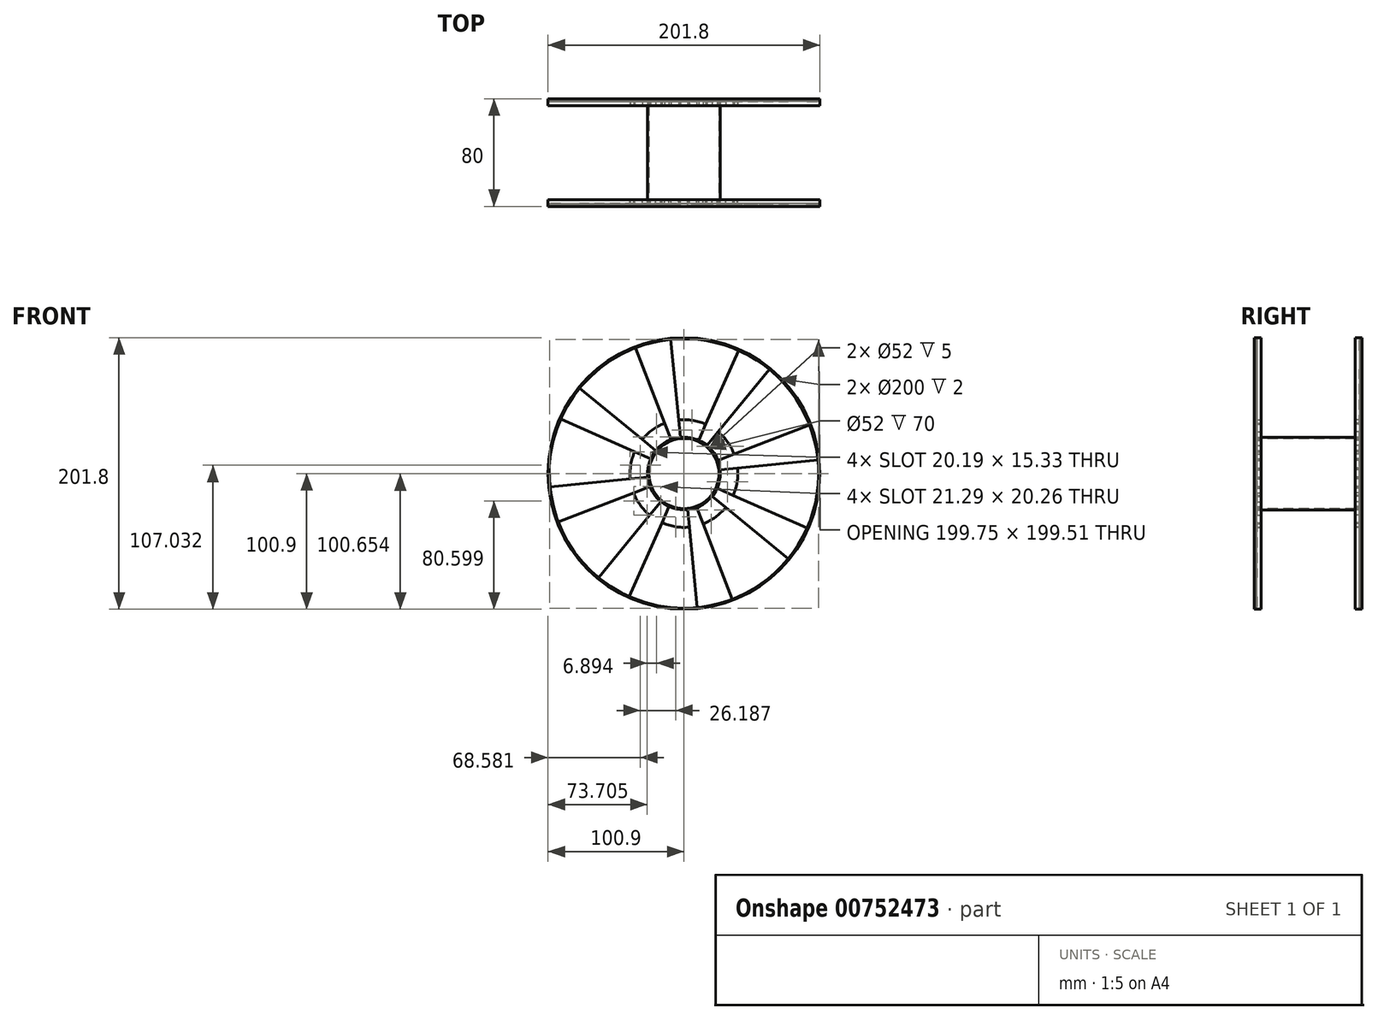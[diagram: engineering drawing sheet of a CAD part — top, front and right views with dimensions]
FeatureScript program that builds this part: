
annotation { "Feature Type Name" : "Feature", "Feature Type Description" : "" }
export const myFeature = defineFeature(function(context is Context, id is Id, definition is map)
    precondition{}
    {
        {
            var Q0;
            Q0=qCreatedBy(makeId("Front.planeOp"),FACE);
            var sketch = newSketch(context, id + "F0", { "sketchPlane" : qUnion([Q0])});
            skCircle(sketch, "E0", {"center": v(0, 0) * mm, "radius": 27 * mm});
            skCircle(sketch, "E1", {"center": v(0, 0) * mm, "radius": 100 * mm});
            skCircle(sketch, "E2", {"center": v(0, 0) * mm, "radius": 40 * mm});
            skLineSegment(sketch, "E3", {"start": v(-20.92, 17.06) * mm, "end": v(-30.95, 25.34) * mm});
            skLineSegment(sketch, "E4", {"start": v(-14.38, 37.33) * mm, "end": v(-9.65, 25.22) * mm});
            skCircle(sketch, "E5", {"center": v(0, 0) * mm, "radius": 100.9 * mm});
            skPoint(sketch, "E6.center", {"position": v(0, -0.02) * mm});
            skLineSegment(sketch, "E7", {"start": v(-14.38, 37.33) * mm, "end": v(-35.95, 93.32) * mm});
            skLineSegment(sketch, "E8", {"start": v(-30.95, 25.34) * mm, "end": v(-77.37, 63.36) * mm});
            skLineSegment(sketch, "E9.1.0", {"start": v(-36.56, 16.23) * mm, "end": v(-91.4, 40.57) * mm});
            skLineSegment(sketch, "E9.1.1", {"start": v(-39.8, -3.96) * mm, "end": v(-99.5, -9.9) * mm});
            skLineSegment(sketch, "E9.1.2", {"start": v(-26.86, -2.73) * mm, "end": v(-39.8, -3.96) * mm});
            skLineSegment(sketch, "E9.1.3", {"start": v(-36.56, 16.23) * mm, "end": v(-24.66, 11) * mm});
            skLineSegment(sketch, "E9.2.0", {"start": v(-37.33, -14.38) * mm, "end": v(-93.32, -35.95) * mm});
            skLineSegment(sketch, "E9.2.1", {"start": v(-25.34, -30.95) * mm, "end": v(-63.36, -77.37) * mm});
            skLineSegment(sketch, "E9.2.2", {"start": v(-17.06, -20.92) * mm, "end": v(-25.34, -30.95) * mm});
            skLineSegment(sketch, "E9.2.3", {"start": v(-37.33, -14.38) * mm, "end": v(-25.22, -9.65) * mm});
            skLineSegment(sketch, "E9.3.0", {"start": v(-16.23, -36.56) * mm, "end": v(-40.57, -91.4) * mm});
            skLineSegment(sketch, "E9.3.1", {"start": v(3.96, -39.8) * mm, "end": v(9.9, -99.5) * mm});
            skLineSegment(sketch, "E9.3.2", {"start": v(2.73, -26.86) * mm, "end": v(3.96, -39.8) * mm});
            skLineSegment(sketch, "E9.3.3", {"start": v(-16.23, -36.56) * mm, "end": v(-11, -24.66) * mm});
            skLineSegment(sketch, "E9.4.0", {"start": v(14.38, -37.33) * mm, "end": v(35.95, -93.32) * mm});
            skLineSegment(sketch, "E9.4.1", {"start": v(30.95, -25.34) * mm, "end": v(77.37, -63.36) * mm});
            skLineSegment(sketch, "E9.4.2", {"start": v(20.92, -17.06) * mm, "end": v(30.95, -25.34) * mm});
            skLineSegment(sketch, "E9.4.3", {"start": v(14.38, -37.33) * mm, "end": v(9.65, -25.22) * mm});
            skLineSegment(sketch, "E9.5.0", {"start": v(36.56, -16.23) * mm, "end": v(91.4, -40.57) * mm});
            skLineSegment(sketch, "E9.5.1", {"start": v(39.8, 3.96) * mm, "end": v(99.5, 9.9) * mm});
            skLineSegment(sketch, "E9.5.2", {"start": v(26.86, 2.73) * mm, "end": v(39.8, 3.96) * mm});
            skLineSegment(sketch, "E9.5.3", {"start": v(36.56, -16.23) * mm, "end": v(24.66, -11) * mm});
            skLineSegment(sketch, "E9.6.0", {"start": v(37.33, 14.38) * mm, "end": v(93.32, 35.95) * mm});
            skLineSegment(sketch, "E9.6.1", {"start": v(25.34, 30.95) * mm, "end": v(63.36, 77.37) * mm});
            skLineSegment(sketch, "E9.6.2", {"start": v(17.06, 20.92) * mm, "end": v(25.34, 30.95) * mm});
            skLineSegment(sketch, "E9.6.3", {"start": v(37.33, 14.38) * mm, "end": v(25.22, 9.65) * mm});
            skLineSegment(sketch, "E9.7.0", {"start": v(16.23, 36.56) * mm, "end": v(40.57, 91.4) * mm});
            skLineSegment(sketch, "E9.7.1", {"start": v(-3.96, 39.8) * mm, "end": v(-9.9, 99.5) * mm});
            skLineSegment(sketch, "E9.7.2", {"start": v(-2.73, 26.86) * mm, "end": v(-3.96, 39.8) * mm});
            skLineSegment(sketch, "E9.7.3", {"start": v(16.23, 36.56) * mm, "end": v(11, 24.66) * mm});
            skCircle(sketch, "E10", {"center": v(0, 0) * mm, "radius": 26 * mm});
            skSolve(sketch);
        }
        {
            var Q0;
            {var subQ0=sQuery(id+"F0.wireOp",EDGE,"E9.4.0");Q0=makeQuery(id+"F0.imprint","IMPRINT",FACE,{"disambiguationData":[TD([[makeQuery(id+"F0.imprint","IMPRINT",EDGE,{"derivedFrom":subQ0}),1.0]])]});}
            var Q1;
            {var subQ0=sQuery(id+"F0.wireOp",EDGE,"E9.2.0");Q1=makeQuery(id+"F0.imprint","IMPRINT",FACE,{"disambiguationData":[TD([[makeQuery(id+"F0.imprint","IMPRINT",EDGE,{"derivedFrom":subQ0}),1.0]])]});}
            var Q2;
            {var subQ0=sQuery(id+"F0.wireOp",EDGE,"E9.5.1");Q2=makeQuery(id+"F0.imprint","IMPRINT",FACE,{"disambiguationData":[TD([[makeQuery(id+"F0.imprint","IMPRINT",EDGE,{"derivedFrom":subQ0}),1.0]])]});}
            var Q3;
            {var subQ0=sQuery(id+"F0.wireOp",EDGE,"E9.1.1");Q3=makeQuery(id+"F0.imprint","IMPRINT",FACE,{"disambiguationData":[TD([[makeQuery(id+"F0.imprint","IMPRINT",EDGE,{"derivedFrom":subQ0}),1.0]])]});}
            var Q4;
            {var subQ0=sQuery(id+"F0.wireOp",EDGE,"E9.5.2");Q4=makeQuery(id+"F0.imprint","IMPRINT",FACE,{"disambiguationData":[TD([[makeQuery(id+"F0.imprint","IMPRINT",EDGE,{"derivedFrom":subQ0}),1.0]])]});}
            var Q5;
            {var subQ0=sQuery(id+"F0.wireOp",EDGE,"E9.6.2");Q5=makeQuery(id+"F0.imprint","IMPRINT",FACE,{"disambiguationData":[TD([[makeQuery(id+"F0.imprint","IMPRINT",EDGE,{"derivedFrom":subQ0}),1.0]])]});}
            var Q6;
            {var subQ0=sQuery(id+"F0.wireOp",EDGE,"E0");var subQ8=makeQuery(id+"F0.imprint","INTERSECT",VERTEX,{"derivedFrom":[subQ0,sQuery(id+"F0.wireOp",EDGE,"E9.5.2")]});Q6=makeQuery(id+"F0.imprint","IMPRINT",FACE,{"disambiguationData":[TD([[makeQuery(id+"F0.imprint","IMPRINT",EDGE,{"disambiguationData":[TD([[subQ8,-1.0]])],"derivedFrom":subQ0}),1.0]])]});}
            var Q7;
            {var subQ0=sQuery(id+"F0.wireOp",EDGE,"E9.4.1");Q7=makeQuery(id+"F0.imprint","IMPRINT",FACE,{"disambiguationData":[TD([[makeQuery(id+"F0.imprint","IMPRINT",EDGE,{"derivedFrom":subQ0}),1.0]])]});}
            var Q8;
            {var subQ0=sQuery(id+"F0.wireOp",EDGE,"E9.4.2");Q8=makeQuery(id+"F0.imprint","IMPRINT",FACE,{"disambiguationData":[TD([[makeQuery(id+"F0.imprint","IMPRINT",EDGE,{"derivedFrom":subQ0}),1.0]])]});}
            var Q9;
            {var subQ0=sQuery(id+"F0.wireOp",EDGE,"E9.2.1");Q9=makeQuery(id+"F0.imprint","IMPRINT",FACE,{"disambiguationData":[TD([[makeQuery(id+"F0.imprint","IMPRINT",EDGE,{"derivedFrom":subQ0}),1.0]])]});}
            var Q10;
            {var subQ0=sQuery(id+"F0.wireOp",EDGE,"E9.3.2");Q10=makeQuery(id+"F0.imprint","IMPRINT",FACE,{"disambiguationData":[TD([[makeQuery(id+"F0.imprint","IMPRINT",EDGE,{"derivedFrom":subQ0}),1.0]])]});}
            var Q11;
            {var subQ0=sQuery(id+"F0.wireOp",EDGE,"E7");Q11=makeQuery(id+"F0.imprint","IMPRINT",FACE,{"disambiguationData":[TD([[makeQuery(id+"F0.imprint","IMPRINT",EDGE,{"derivedFrom":subQ0}),-1.0]])]});}
            var Q12;
            {var subQ0=sQuery(id+"F0.wireOp",EDGE,"E9.1.2");Q12=makeQuery(id+"F0.imprint","IMPRINT",FACE,{"disambiguationData":[TD([[makeQuery(id+"F0.imprint","IMPRINT",EDGE,{"derivedFrom":subQ0}),1.0]])]});}
            var Q13;
            {var subQ0=sQuery(id+"F0.wireOp",EDGE,"E8");Q13=makeQuery(id+"F0.imprint","IMPRINT",FACE,{"disambiguationData":[TD([[makeQuery(id+"F0.imprint","IMPRINT",EDGE,{"derivedFrom":subQ0}),1.0]])]});}
            var Q14;
            {var subQ0=sQuery(id+"F0.wireOp",EDGE,"E9.2.2");Q14=makeQuery(id+"F0.imprint","IMPRINT",FACE,{"disambiguationData":[TD([[makeQuery(id+"F0.imprint","IMPRINT",EDGE,{"derivedFrom":subQ0}),1.0]])]});}
            var Q15;
            {var subQ0=sQuery(id+"F0.wireOp",EDGE,"E9.3.1");Q15=makeQuery(id+"F0.imprint","IMPRINT",FACE,{"disambiguationData":[TD([[makeQuery(id+"F0.imprint","IMPRINT",EDGE,{"derivedFrom":subQ0}),1.0]])]});}
            var Q16;
            {var subQ0=sQuery(id+"F0.wireOp",EDGE,"E9.1.0");Q16=makeQuery(id+"F0.imprint","IMPRINT",FACE,{"disambiguationData":[TD([[makeQuery(id+"F0.imprint","IMPRINT",EDGE,{"derivedFrom":subQ0}),1.0]])]});}
            var Q17;
            {var subQ0=sQuery(id+"F0.wireOp",EDGE,"E9.3.0");Q17=makeQuery(id+"F0.imprint","IMPRINT",FACE,{"disambiguationData":[TD([[makeQuery(id+"F0.imprint","IMPRINT",EDGE,{"derivedFrom":subQ0}),1.0]])]});}
            var Q18;
            {var subQ0=sQuery(id+"F0.wireOp",EDGE,"E9.6.1");Q18=makeQuery(id+"F0.imprint","IMPRINT",FACE,{"disambiguationData":[TD([[makeQuery(id+"F0.imprint","IMPRINT",EDGE,{"derivedFrom":subQ0}),1.0]])]});}
            var Q19;
            {var subQ0=sQuery(id+"F0.wireOp",EDGE,"E9.5.0");Q19=makeQuery(id+"F0.imprint","IMPRINT",FACE,{"disambiguationData":[TD([[makeQuery(id+"F0.imprint","IMPRINT",EDGE,{"derivedFrom":subQ0}),1.0]])]});}
            var Q20;
            {var subQ0=sQuery(id+"F0.wireOp",EDGE,"E7");Q20=makeQuery(id+"F0.imprint","IMPRINT",FACE,{"disambiguationData":[TD([[makeQuery(id+"F0.imprint","IMPRINT",EDGE,{"derivedFrom":subQ0}),1.0]])]});}
            var Q21;
            {var subQ0=sQuery(id+"F0.wireOp",EDGE,"E3");Q21=makeQuery(id+"F0.imprint","IMPRINT",FACE,{"disambiguationData":[TD([[makeQuery(id+"F0.imprint","IMPRINT",EDGE,{"derivedFrom":subQ0}),1.0]])]});}
            var Q22;
            {var subQ0=sQuery(id+"F0.wireOp",EDGE,"E9.7.0");Q22=makeQuery(id+"F0.imprint","IMPRINT",FACE,{"disambiguationData":[TD([[makeQuery(id+"F0.imprint","IMPRINT",EDGE,{"derivedFrom":subQ0}),1.0]])]});}
            var Q23;
            {var subQ0=sQuery(id+"F0.wireOp",EDGE,"E9.6.0");Q23=makeQuery(id+"F0.imprint","IMPRINT",FACE,{"disambiguationData":[TD([[makeQuery(id+"F0.imprint","IMPRINT",EDGE,{"derivedFrom":subQ0}),1.0]])]});}
            var Q24;
            {var subQ0=sQuery(id+"F0.wireOp",EDGE,"E4");Q24=makeQuery(id+"F0.imprint","IMPRINT",FACE,{"disambiguationData":[TD([[makeQuery(id+"F0.imprint","IMPRINT",EDGE,{"derivedFrom":subQ0}),1.0]])]});}
            var Q25;
            Q25=makeQuery(id+"F0.imprint","IMPRINT",FACE,{"disambiguationData":[TD([[makeQuery(id+"F0.imprint","IMPRINT",EDGE,{"derivedFrom":sQuery(id+"F0.wireOp",EDGE,"E5")}),1.0]])]});
            extrude(context, id + "F1", {"entities" : qUnion([Q0, Q1, Q2, Q3, Q4, Q5, Q6, Q7, Q8, Q9, Q10, Q11, Q12, Q13, Q14, Q15, Q16, Q17, Q18, Q19, Q20, Q21, Q22, Q23, Q24, Q25]), "depth" : 3 * mm, "offsetDistance" : 25 * mm});
        }
        {
            var Q0;
            Q0=makeQuery(id+"F0.imprint","IMPRINT",FACE,{"disambiguationData":[TD([[makeQuery(id+"F0.imprint","IMPRINT",EDGE,{"derivedFrom":sQuery(id+"F0.wireOp",EDGE,"E5")}),1.0]])]});
            extrude(context, id + "F2", {"entities" : qUnion([Q0]), "operationType" : NewBodyOperationType.ADD, "depth" : 5 * mm, "offsetDistance" : 25 * mm});
        }
        {
            var Q0;
            {var subQ0=sQuery(id+"F0.wireOp",EDGE,"E8");Q0=makeQuery(id+"F0.imprint","IMPRINT",FACE,{"disambiguationData":[TD([[makeQuery(id+"F0.imprint","IMPRINT",EDGE,{"derivedFrom":subQ0}),1.0]])]});}
            var Q1;
            {var subQ0=sQuery(id+"F0.wireOp",EDGE,"E9.1.1");Q1=makeQuery(id+"F0.imprint","IMPRINT",FACE,{"disambiguationData":[TD([[makeQuery(id+"F0.imprint","IMPRINT",EDGE,{"derivedFrom":subQ0}),1.0]])]});}
            var Q2;
            {var subQ0=sQuery(id+"F0.wireOp",EDGE,"E9.2.1");Q2=makeQuery(id+"F0.imprint","IMPRINT",FACE,{"disambiguationData":[TD([[makeQuery(id+"F0.imprint","IMPRINT",EDGE,{"derivedFrom":subQ0}),1.0]])]});}
            var Q3;
            {var subQ0=sQuery(id+"F0.wireOp",EDGE,"E9.3.1");Q3=makeQuery(id+"F0.imprint","IMPRINT",FACE,{"disambiguationData":[TD([[makeQuery(id+"F0.imprint","IMPRINT",EDGE,{"derivedFrom":subQ0}),1.0]])]});}
            var Q4;
            {var subQ0=sQuery(id+"F0.wireOp",EDGE,"E9.4.1");Q4=makeQuery(id+"F0.imprint","IMPRINT",FACE,{"disambiguationData":[TD([[makeQuery(id+"F0.imprint","IMPRINT",EDGE,{"derivedFrom":subQ0}),1.0]])]});}
            var Q5;
            {var subQ0=sQuery(id+"F0.wireOp",EDGE,"E9.5.1");Q5=makeQuery(id+"F0.imprint","IMPRINT",FACE,{"disambiguationData":[TD([[makeQuery(id+"F0.imprint","IMPRINT",EDGE,{"derivedFrom":subQ0}),1.0]])]});}
            var Q6;
            {var subQ0=sQuery(id+"F0.wireOp",EDGE,"E9.6.1");Q6=makeQuery(id+"F0.imprint","IMPRINT",FACE,{"disambiguationData":[TD([[makeQuery(id+"F0.imprint","IMPRINT",EDGE,{"derivedFrom":subQ0}),1.0]])]});}
            var Q7;
            {var subQ0=sQuery(id+"F0.wireOp",EDGE,"E7");Q7=makeQuery(id+"F0.imprint","IMPRINT",FACE,{"disambiguationData":[TD([[makeQuery(id+"F0.imprint","IMPRINT",EDGE,{"derivedFrom":subQ0}),-1.0]])]});}
            var Q8;
            {var subQ0=sQuery(id+"F0.wireOp",EDGE,"E9.2.2");Q8=makeQuery(id+"F0.imprint","IMPRINT",FACE,{"disambiguationData":[TD([[makeQuery(id+"F0.imprint","IMPRINT",EDGE,{"derivedFrom":subQ0}),1.0]])]});}
            var Q9;
            {var subQ0=sQuery(id+"F0.wireOp",EDGE,"E9.3.2");Q9=makeQuery(id+"F0.imprint","IMPRINT",FACE,{"disambiguationData":[TD([[makeQuery(id+"F0.imprint","IMPRINT",EDGE,{"derivedFrom":subQ0}),1.0]])]});}
            var Q10;
            {var subQ0=sQuery(id+"F0.wireOp",EDGE,"E9.4.2");Q10=makeQuery(id+"F0.imprint","IMPRINT",FACE,{"disambiguationData":[TD([[makeQuery(id+"F0.imprint","IMPRINT",EDGE,{"derivedFrom":subQ0}),1.0]])]});}
            var Q11;
            {var subQ0=sQuery(id+"F0.wireOp",EDGE,"E9.5.2");Q11=makeQuery(id+"F0.imprint","IMPRINT",FACE,{"disambiguationData":[TD([[makeQuery(id+"F0.imprint","IMPRINT",EDGE,{"derivedFrom":subQ0}),1.0]])]});}
            var Q12;
            {var subQ0=sQuery(id+"F0.wireOp",EDGE,"E9.6.2");Q12=makeQuery(id+"F0.imprint","IMPRINT",FACE,{"disambiguationData":[TD([[makeQuery(id+"F0.imprint","IMPRINT",EDGE,{"derivedFrom":subQ0}),1.0]])]});}
            var Q13;
            {var subQ0=sQuery(id+"F0.wireOp",EDGE,"E4");Q13=makeQuery(id+"F0.imprint","IMPRINT",FACE,{"disambiguationData":[TD([[makeQuery(id+"F0.imprint","IMPRINT",EDGE,{"derivedFrom":subQ0}),1.0]])]});}
            var Q14;
            {var subQ0=sQuery(id+"F0.wireOp",EDGE,"E9.1.2");Q14=makeQuery(id+"F0.imprint","IMPRINT",FACE,{"disambiguationData":[TD([[makeQuery(id+"F0.imprint","IMPRINT",EDGE,{"derivedFrom":subQ0}),1.0]])]});}
            var Q15;
            {var subQ0=sQuery(id+"F0.wireOp",EDGE,"E3");Q15=makeQuery(id+"F0.imprint","IMPRINT",FACE,{"disambiguationData":[TD([[makeQuery(id+"F0.imprint","IMPRINT",EDGE,{"derivedFrom":subQ0}),1.0]])]});}
            extrude(context, id + "F3", {"entities" : qUnion([Q0, Q1, Q2, Q3, Q4, Q5, Q6, Q7, Q8, Q9, Q10, Q11, Q12, Q13, Q14, Q15]), "operationType" : NewBodyOperationType.ADD, "depth" : 4 * mm, "offsetDistance" : 25 * mm});
        }
        {
            var Q0;
            {var subQ0=sQuery(id+"F0.wireOp",EDGE,"E9.6.2");var subQ1=sQuery(id+"F0.wireOp",EDGE,"E9.5.3");var subQ2=sQuery(id+"F0.wireOp",EDGE,"E9.1.3");var subQ3=sQuery(id+"F0.wireOp",EDGE,"E4");var subQ4=sQuery(id+"F0.wireOp",EDGE,"E3");var subQ5=sQuery(id+"F0.wireOp",EDGE,"E9.4.2");var subQ6=sQuery(id+"F0.wireOp",EDGE,"E0");var subQ9=sQuery(id+"F0.wireOp",EDGE,"E9.3.2");var subQ11=sQuery(id+"F0.wireOp",EDGE,"E9.4.3");var subQ13=sQuery(id+"F0.wireOp",EDGE,"E9.2.2");var subQ15=sQuery(id+"F0.wireOp",EDGE,"E9.3.3");var subQ17=sQuery(id+"F0.wireOp",EDGE,"E9.7.2");var subQ18=sQuery(id+"F0.wireOp",EDGE,"E9.1.2");var subQ20=sQuery(id+"F0.wireOp",EDGE,"E9.2.3");var subQ24=sQuery(id+"F0.wireOp",EDGE,"E9.5.2");var subQ25=sQuery(id+"F0.wireOp",EDGE,"E10");var subQ28=sQuery(id+"F0.wireOp",EDGE,"E9.7.3");var subQ30=sQuery(id+"F0.wireOp",EDGE,"E9.6.3");Q0=makeQuery(id+"F3.boolean.opBoolean","SPLIT",FACE,{"disambiguationData":[TD([makeQuery(id+"F1.opExtrude","SWEPT_FACE",FACE,{"disambiguationData":[OSD([subQ25])]})])],"derivedFrom":makeQuery(id+"F1.opExtrude","CAP_FACE",FACE,{"disambiguationData":[OSD([subQ6,sQuery(id+"F0.wireOp",EDGE,"E2"),subQ4,subQ3,sQuery(id+"F0.wireOp",EDGE,"E5"),subQ18,subQ2,subQ13,subQ20,subQ9,subQ15,subQ5,subQ11,subQ24,subQ1,subQ0,subQ30,subQ17,subQ28,subQ25])],"isStart":false})});}
            var Q1;
            Q1=sQuery(id+"F0.wireOp",EDGE,"E10");
            var Q2;
            Q2=sQuery(id+"F0.wireOp",EDGE,"E0");
            extrude(context, id + "F4", {"entities" : qUnion([Q0]), "operationType" : NewBodyOperationType.ADD, "surfaceEntities" : qUnion([Q1, Q2]), "depth" : 2 * mm, "offsetDistance" : 25 * mm});
        }
        {
            var Q0;
            Q0=makeQuery(id+"F1.opExtrude","SWEPT_BODY",BODY,{"disambiguationData":[OSD([sQuery(id+"F0.wireOp",EDGE,"E0"),sQuery(id+"F0.wireOp",EDGE,"E2"),sQuery(id+"F0.wireOp",EDGE,"E3"),sQuery(id+"F0.wireOp",EDGE,"E4"),sQuery(id+"F0.wireOp",EDGE,"E5"),sQuery(id+"F0.wireOp",EDGE,"E9.1.2"),sQuery(id+"F0.wireOp",EDGE,"E9.1.3"),sQuery(id+"F0.wireOp",EDGE,"E9.2.2"),sQuery(id+"F0.wireOp",EDGE,"E9.2.3"),sQuery(id+"F0.wireOp",EDGE,"E9.3.2"),sQuery(id+"F0.wireOp",EDGE,"E9.3.3"),sQuery(id+"F0.wireOp",EDGE,"E9.4.2"),sQuery(id+"F0.wireOp",EDGE,"E9.4.3"),sQuery(id+"F0.wireOp",EDGE,"E9.5.2"),sQuery(id+"F0.wireOp",EDGE,"E9.5.3"),sQuery(id+"F0.wireOp",EDGE,"E9.6.2"),sQuery(id+"F0.wireOp",EDGE,"E9.6.3"),sQuery(id+"F0.wireOp",EDGE,"E9.7.2"),sQuery(id+"F0.wireOp",EDGE,"E9.7.3"),sQuery(id+"F0.wireOp",EDGE,"E10")])]});
            var Q1;
            Q1=qCreatedBy(makeId("Front.planeOp"),FACE);
            mirror(context, id + "F5", {"entities" : qUnion([Q0]), "mirrorPlane" : qUnion([Q1])});
        }
        {
            var Q0;
            Q0=makeQuery(id+"F5.opPattern","COPY",BODY,{"derivedFrom":makeQuery(id+"F1.opExtrude","SWEPT_BODY",BODY,{"disambiguationData":[OSD([sQuery(id+"F0.wireOp",EDGE,"E0"),sQuery(id+"F0.wireOp",EDGE,"E2"),sQuery(id+"F0.wireOp",EDGE,"E3"),sQuery(id+"F0.wireOp",EDGE,"E4"),sQuery(id+"F0.wireOp",EDGE,"E5"),sQuery(id+"F0.wireOp",EDGE,"E9.1.2"),sQuery(id+"F0.wireOp",EDGE,"E9.1.3"),sQuery(id+"F0.wireOp",EDGE,"E9.2.2"),sQuery(id+"F0.wireOp",EDGE,"E9.2.3"),sQuery(id+"F0.wireOp",EDGE,"E9.3.2"),sQuery(id+"F0.wireOp",EDGE,"E9.3.3"),sQuery(id+"F0.wireOp",EDGE,"E9.4.2"),sQuery(id+"F0.wireOp",EDGE,"E9.4.3"),sQuery(id+"F0.wireOp",EDGE,"E9.5.2"),sQuery(id+"F0.wireOp",EDGE,"E9.5.3"),sQuery(id+"F0.wireOp",EDGE,"E9.6.2"),sQuery(id+"F0.wireOp",EDGE,"E9.6.3"),sQuery(id+"F0.wireOp",EDGE,"E9.7.2"),sQuery(id+"F0.wireOp",EDGE,"E9.7.3"),sQuery(id+"F0.wireOp",EDGE,"E10")])]}),"instanceName":"1"});
            transform(context, id + "F6", {"entities" : qUnion([Q0]), "transformType" : TransformType.TRANSLATION_3D, "dx" : 0 * mm, "dy" : 70 * mm, "dz" : 0 * mm, "makeCopy" : false});
        }
        {
            var Q0;
            Q0=makeQuery(id+"F0.imprint","IMPRINT",FACE,{"disambiguationData":[TD([[makeQuery(id+"F0.imprint","IMPRINT",EDGE,{"derivedFrom":sQuery(id+"F0.wireOp",EDGE,"E10")}),-1.0]])]});
            extrude(context, id + "F7", {"entities" : qUnion([Q0]), "oppositeDirection" : true, "depth" : 70 * mm, "offsetDistance" : 25 * mm});
        }
    });
